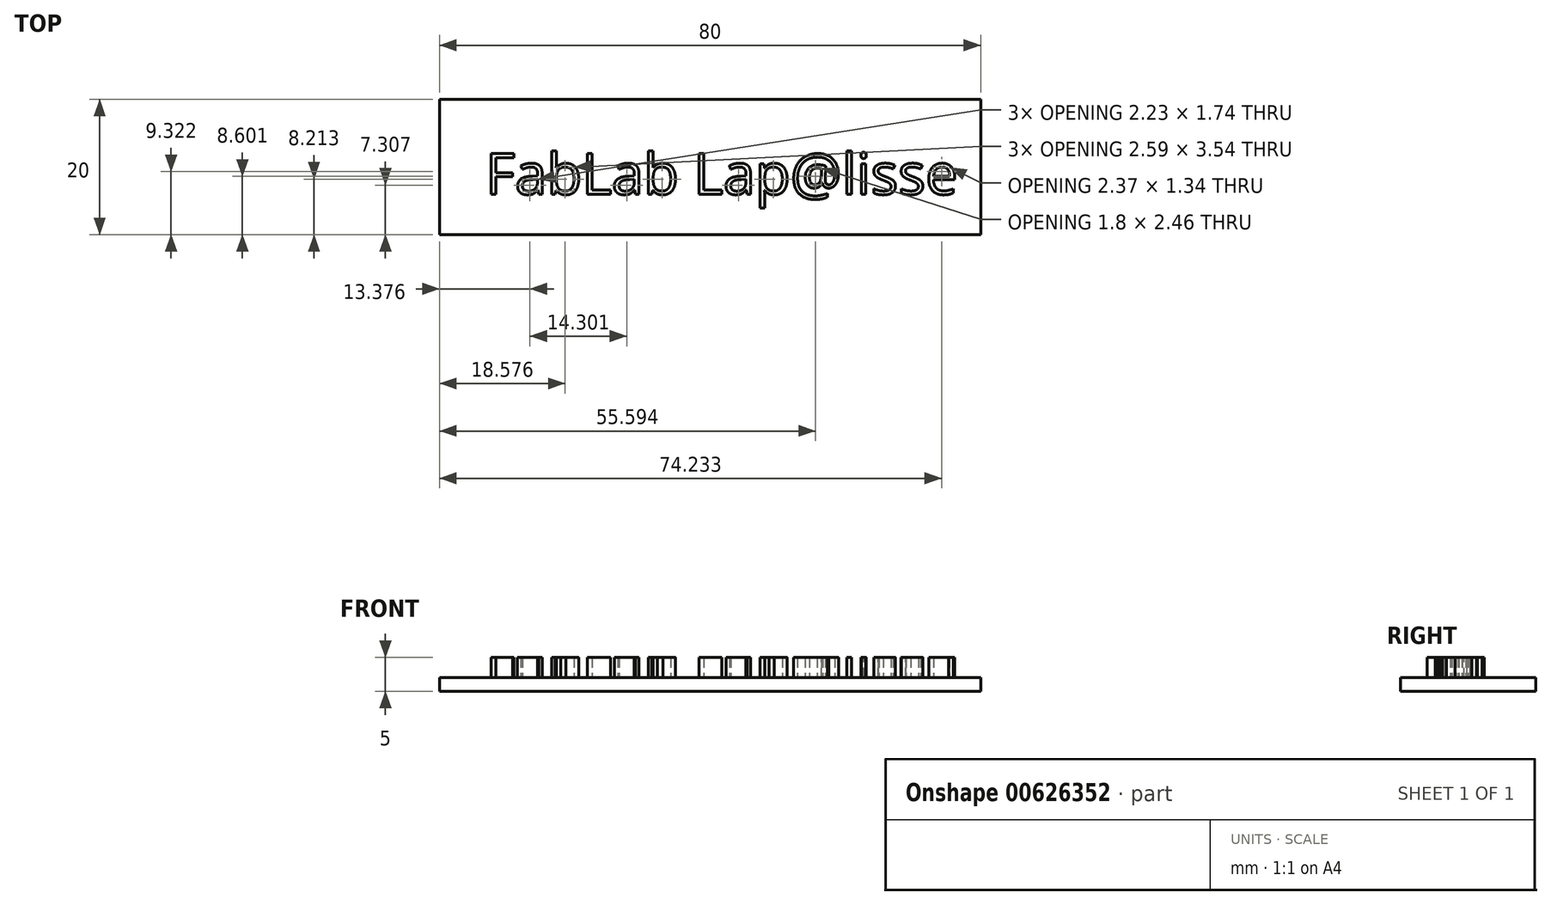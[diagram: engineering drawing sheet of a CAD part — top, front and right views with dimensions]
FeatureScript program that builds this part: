
annotation { "Feature Type Name" : "Feature", "Feature Type Description" : "" }
export const myFeature = defineFeature(function(context is Context, id is Id, definition is map)
    precondition{}
    {
        {
            var Q0;
            Q0=qCreatedBy(makeId("Top.planeOp"),FACE);
            var sketch = newSketch(context, id + "F0", { "sketchPlane" : qUnion([Q0])});
            skText(sketch, "E0", { "text": "FabLab Lap@lisse", "fontName": "OpenSans-Regular.ttf"});
            const initialGuessF0  = {"E0": [-0.00192, -0.0024, 1, 0, 0.0061]};
            skSetInitialGuess(sketch, initialGuessF0);
            skSolve(sketch);
        }
        {
            var Q0;
            Q0 = qSketchRegion(id + "F0", true);
            extrude(context, id + "F1", {"entities" : qUnion([Q0]), "depth" : 3 * mm, "offsetDistance" : 25 * mm});
        }
        {
            var Q0;
            Q0=qCreatedBy(makeId("Top.planeOp"),FACE);
            var sketch = newSketch(context, id + "F2", { "sketchPlane" : qUnion([Q0])});
            skLineSegment(sketch, "E1.bottom", {"start": v(-8.7, 11.65) * mm, "end": v(71.3, 11.65) * mm});
            skLineSegment(sketch, "E1.top", {"start": v(-8.7, -8.35) * mm, "end": v(71.3, -8.35) * mm});
            skLineSegment(sketch, "E1.left", {"start": v(-8.7, 11.65) * mm, "end": v(-8.7, -8.35) * mm});
            skLineSegment(sketch, "E1.right", {"start": v(71.3, 11.65) * mm, "end": v(71.3, -8.35) * mm});
            skSolve(sketch);
        }
        {
            var Q0;
            Q0 = qSketchRegion(id + "F2", true);
            extrude(context, id + "F3", {"entities" : qUnion([Q0]), "oppositeDirection" : true, "depth" : 2 * mm, "offsetDistance" : 25 * mm});
        }
    });
